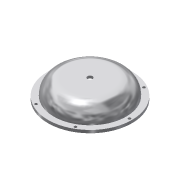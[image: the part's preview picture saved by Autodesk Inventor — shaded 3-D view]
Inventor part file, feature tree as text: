
AUTODESK INVENTOR PART (.ipt)
format: ipt  version: 2015 (Build 190159000, 159)  size: 191,488 bytes
history: native  units: mm
features: sketch x3, projected_geometry x3, extrude x2, fillet x2, revolve x1, hole x1, pattern_circular x1, plane x1
ambient origin geometry x8: Origin, YZ Plane, XZ Plane, XY Plane, X Axis, Y Axis, Z Axis, Center Point
bodies: Body1 (feature_tree)
feature tree (14):
  revolve  "Umdrehung4"
  extrude  "Extrusion10"  Depth=10.0mm
  extrude  "Extrusion11"  Depth=3.0mm
  hole  "Bohrung3"  [1 undecoded]
  pattern_circular  "Runde Anordnung2"  [2 undecoded]
  plane  "Arbeitsebene10"
  fillet  "Rundung1"  Radius=102.0mm
  fillet  "Rundung2"  Radius=7.0mm
  sketch  "Skizze28"  dims[d103=10.0mm d143=6.2mm]
  projected_geometry  "Projizierte Kontur8"
  sketch  "Skizze29"  dims[d146=18.0mm d147=3.0mm]
  projected_geometry  "Projizierte Kontur9"
  sketch  "Skizze30"  dims[d148=90.0deg d155=5.0mm d156=4.0mm d157=102.0mm d158=7.0mm d159=0.0mm d160=86.0mm d161=3.5mm d162=0.0mm d163=48.0mm d164=3.3mm d165=6.0mm d166=4.0mm d167=2.0mm d168=90.0deg d169=8.0mm d170=20.594885mm d171=60.0mm d172=360.0deg d174=17.0mm d186=80.0mm d187=15.0mm d188=18.0mm d135=1.0mm d136=1.0mm]
  projected_geometry  "Projizierte Kontur10"
note: 3 required parameter values undecoded (feature->parameter linkage not recoverable at this tier; creation-order binding heuristic only, values carry confidence <= 0.55)
